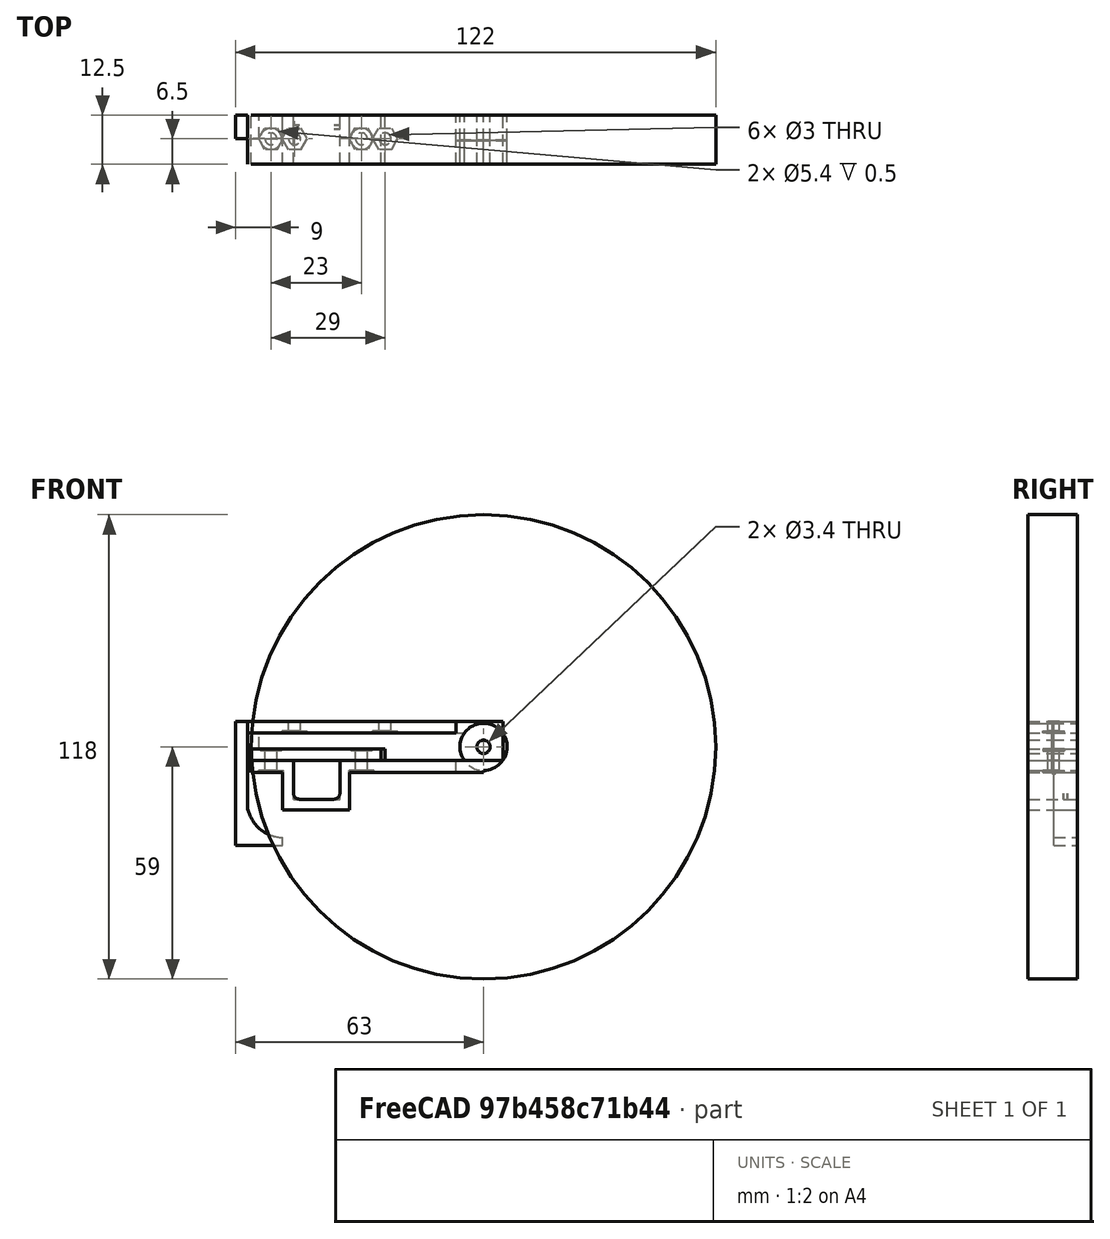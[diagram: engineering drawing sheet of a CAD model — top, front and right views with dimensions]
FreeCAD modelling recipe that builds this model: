
FCSTD DOCUMENT  (FreeCAD 0.18R16131 (Git))
Label: Soporte Motor 1
License: All rights reserved
LicenseURL: http://en.wikipedia.org/wiki/All_rights_reserved
objects: Part::Box×13, Part::Cylinder×13, Part::MultiFuse×11, Part::Cut×11, Part::Extrusion×6, Part::RegularPolygon×4, Part::Circle×2, Part::Fillet×1
note: 61 computed .brp shape members not serialized (recipe doc carries the construction recipe); baked Part::Feature solids carry a one-line shape summary decoded from their .brp

FEATURE [Part::Box] Box  label="Cubo"
  AttacherType = Attacher::AttachEngine3D
  Height = 12.6
  Length = 17
  Placement = pos=(-1,0,-1) rot=(0,0,1;0rad)
  Width = 12.5
FEATURE [Part::Box] Box001  label="Cubo001"
  AttacherType = Attacher::AttachEngine3D
  Height = 10
  Length = 11.8
  Placement = pos=(1.7,0,1.7) rot=(0,0,1;0rad)
  Width = 12.5
FEATURE [Part::Fillet] Fillet
  Base = -> Box001
  Edges = 2 edges r=1.5: [Edge4,Edge8]
FEATURE [Part::Box] Box002  label="Cubo002"
  AttacherType = Attacher::AttachEngine3D
  Height = 10
  Length = 11.8
  Placement = pos=(1.7,9,1.7) rot=(0,0,1;0rad)
  Width = 1
FEATURE [Part::Box] Box003  label="Cubo003"
  AttacherType = Attacher::AttachEngine3D
  Height = 10
  Length = 65
  Placement = pos=(-10,0,11.5) rot=(0,0,1;0rad)
  Width = 12.5
FEATURE [Part::Cylinder] Cylinder  label="Eje 1"
  Angle = 360
  AttacherType = Attacher::AttachEngine3D
  Height = 3
  Placement = pos=(50,0,15) rot=(-1,0,0;1.5708rad)
  Radius = 6
FEATURE [Part::Box] Box004  label="Cubo004"
  AttacherType = Attacher::AttachEngine3D
  Height = 3
  Length = 59
  Placement = pos=(-9,0,8.5) rot=(0,0,1;0rad)
  Width = 12.5
FEATURE [Part::Box] Box005  label="Cubo005"
  AttacherType = Attacher::AttachEngine3D
  Height = 3
  Length = 53
  Placement = pos=(-10,0,18.5) rot=(0,0,1;0rad)
  Width = 12.5
FEATURE [Part::Box] Box006  label="Cubo006"
  AttacherType = Attacher::AttachEngine3D
  Height = 3
  Length = 35
  Placement = pos=(-10,0,11.5) rot=(0,0,1;0rad)
  Width = 12.5
FEATURE [Part::Box] Box007  label="Tapa sin taladros"
  AttacherType = Attacher::AttachEngine3D
  Height = 3
  Length = 33
  Placement = pos=(-9,0,11.5) rot=(0,0,1;0rad)
  Width = 12.5
FEATURE [Part::Cylinder] Cylinder001  label="Taladro 1"
  Angle = 360
  AttacherType = Attacher::AttachEngine3D
  Height = 24
  Placement = pos=(-4,6.5,0) rot=(0,0,1;0rad)
  Radius = 1.5
FEATURE [Part::Cylinder] Cylinder002  label="Taladro 2"
  Angle = 360
  AttacherType = Attacher::AttachEngine3D
  Height = 24
  Placement = pos=(19,6.5,0) rot=(0,0,1;0rad)
  Radius = 1.5
FEATURE [Part::Box] Box008  label="Cubo008"
  AttacherType = Attacher::AttachEngine3D
  Height = 31.5
  Length = 3
  Placement = pos=(-13,3.2,-10) rot=(0,0,1;0rad)
  Width = 6
FEATURE [Part::Box] Box009  label="Cubo009"
  AttacherType = Attacher::AttachEngine3D
  Height = 9
  Length = 9
  Placement = pos=(-10,3.2,-10) rot=(0,0,1;0rad)
  Width = 6
FEATURE [Part::Box] Box010  label="Cubo010"
  AttacherType = Attacher::AttachEngine3D
  Height = 4
  Length = 3
  Placement = pos=(-10,3.2,14.5) rot=(0,0,1;0rad)
  Width = 6
FEATURE [Part::Cylinder] Cylinder003  label="Cilindro001"
  Angle = 360
  AttacherType = Attacher::AttachEngine3D
  Height = 12.5
  Placement = pos=(50,0,15) rot=(-1,0,0;1.5708rad)
  Radius = 59
FEATURE [Part::Cylinder] Cylinder004  label="Taladro 3"
  Angle = 360
  AttacherType = Attacher::AttachEngine3D
  Height = 20.5
  Placement = pos=(50,-3,15) rot=(-1,0,0;1.5708rad)
  Radius = 1.7
FEATURE [Part::Cylinder] Cylinder005  label="Eje 2"
  Angle = 360
  AttacherType = Attacher::AttachEngine3D
  Height = 3
  Placement = pos=(50,3,15) rot=(-1,0,0;1.5708rad)
  Radius = 6
FEATURE [Part::Cylinder] Cylinder006  label="Eje 3"
  Angle = 360
  AttacherType = Attacher::AttachEngine3D
  Height = 6.4
  Placement = pos=(50,6.1,15) rot=(-1,0,0;1.5708rad)
  Radius = 6
FEATURE [Part::Box] Box011  label="Cubo011"
  AttacherType = Attacher::AttachEngine3D
  Height = 3
  Length = 60
  Placement = pos=(-10,6.1,18.5) rot=(0,0,1;0rad)
  Width = 6.4
FEATURE [Part::MultiFuse] Fusion  label="Base superior"
  Shapes = -> [Box011,Box005,Cylinder006]
FEATURE [Part::Box] Box012  label="Ranura Eje"
  AttacherType = Attacher::AttachEngine3D
  Height = 3
  Length = 7
  Placement = pos=(43,6,8.5) rot=(0,0,1;0rad)
  Width = 6.5
FEATURE [Part::Cut] Cut
  Base = -> Box004
  Tool = -> Box012
FEATURE [Part::MultiFuse] Fusion001  label="Base Inferior"
  Shapes = -> [Cylinder,Cylinder005,Cut,Box]
FEATURE [Part::MultiFuse] Fusion002  label="Hueco Motor"
  Shapes = -> [Fillet,Box002]
FEATURE [Part::Cut] Cut001  label="Base Inferior 2"
  Base = -> Fusion001
  Tool = -> Fusion002
FEATURE [Part::MultiFuse] Fusion003  label="Trasera Superior"
  Placement = pos=(0,3.3,0) rot=(0,0,1;0rad)
  Shapes = -> [Box008,Box009,Box010]
FEATURE [Part::MultiFuse] Fusion004  label="Base Superior 2"
  Shapes = -> [Fusion,Fusion003]
FEATURE [Part::Cylinder] Cylinder007  label="Taladro 004"
  Angle = 360
  AttacherType = Attacher::AttachEngine3D
  Height = 20.5
  Placement = pos=(50,-3,15) rot=(-1,0,0;1.5708rad)
  Radius = 1.7
FEATURE [Part::Cut] Cut002  label="Base Superior con eje"
  Base = -> Fusion004
  Tool = -> Cylinder004
FEATURE [Part::Cut] Cut003  label="Base Inferior con eje"
  Base = -> Cut001
  Tool = -> Cylinder007
FEATURE [Part::Cylinder] Cylinder008  label="Taladro 1b"
  Angle = 360
  AttacherType = Attacher::AttachEngine3D
  Height = 24
  Placement = pos=(-4,6.5,0) rot=(0,0,1;0rad)
  Radius = 1.5
FEATURE [Part::Cylinder] Cylinder009  label="Taladro 1c"
  Angle = 360
  AttacherType = Attacher::AttachEngine3D
  Height = 24
  Placement = pos=(-4,6.5,0) rot=(0,0,1;0rad)
  Radius = 1.5
FEATURE [Part::Cylinder] Cylinder010  label="Taladro 2b"
  Angle = 360
  AttacherType = Attacher::AttachEngine3D
  Height = 24
  Placement = pos=(19,6.5,0) rot=(0,0,1;0rad)
  Radius = 1.5
FEATURE [Part::Cylinder] Cylinder011  label="Taladro 2c"
  Angle = 360
  AttacherType = Attacher::AttachEngine3D
  Height = 24
  Placement = pos=(19,6.5,0) rot=(0,0,1;0rad)
  Radius = 1.5
FEATURE [Part::MultiFuse] Fusion005  label="Taladros superiores"
  Placement = pos=(6,0,0) rot=(0,0,1;0rad)
  Shapes = -> [Cylinder001,Cylinder002]
FEATURE [Part::MultiFuse] Fusion006  label="Taladros inferiores"
  Shapes = -> [Cylinder008,Cylinder010]
FEATURE [Part::MultiFuse] Fusion007  label="Taladros tapa"
  Shapes = -> [Cylinder009,Cylinder011]
FEATURE [Part::Cut] Cut004  label="Base superior mal"
  Base = -> Cut002
  Tool = -> Fusion005
FEATURE [Part::Cut] Cut005  label="Base inferior taladrada"
  Base = -> Cut003
  Tool = -> Fusion006
FEATURE [Part::Cut] Cut006  label="Tapa taladrada"
  Base = -> Box007
  Tool = -> Fusion007
FEATURE [Part::Cylinder] Cylinder012  label="Cilindro"
  Angle = 360
  AttacherType = Attacher::AttachEngine3D
  Height = 20
  Placement = pos=(-1,0,1) rot=(-1,0,0;1.5708rad)
  Radius = 9
FEATURE [Part::Cut] Cut007  label="Base superior taladrada"
  Base = -> Cut004
  Tool = -> Cylinder012
FEATURE [Part::RegularPolygon] RegularPolygon  label="Polígono regular"
  AttacherType = Attacher::AttachEngine3D
  Circumradius = 3.15
  Placement = pos=(19,6.5,8) rot=(0,0,1;0rad)
  Polygon = 6
FEATURE [Part::RegularPolygon] RegularPolygon001  label="Polígono regular001"
  AttacherType = Attacher::AttachEngine3D
  Circumradius = 3.15
  Placement = pos=(-4,6.5,8) rot=(0,0,1;0rad)
  Polygon = 6
FEATURE [Part::Extrusion] Extrude  label="Agujero tuerca 1"
  Base = -> RegularPolygon
  Dir = (0,0,1)
  DirMode = 2
  FaceMakerClass = Part::FaceMakerBullseye
  LengthFwd = 1
  LengthRev = 0
  Solid = true
  Symmetric = false
FEATURE [Part::Extrusion] Extrude001  label="Agujero tuerca 2"
  Base = -> RegularPolygon001
  Dir = (0,0,1)
  DirMode = 2
  FaceMakerClass = Part::FaceMakerBullseye
  LengthFwd = 1
  LengthRev = 0
  Solid = true
  Symmetric = false
FEATURE [Part::MultiFuse] Fusion008
  Shapes = -> [Extrude,Extrude001]
FEATURE [Part::Cut] Cut008  label="Base inferior tuercas"
  Base = -> Cut005
  Tool = -> Fusion008
FEATURE [Part::Circle] Circle  label="Circunferencia"
  Angle0 = 0
  Angle1 = 360
  AttacherType = Attacher::AttachEngine3D
  Placement = pos=(-4,6.5,15) rot=(0,0,1;0rad)
  Radius = 2.7
FEATURE [Part::Circle] Circle001  label="Circunferencia001"
  Angle0 = 0
  Angle1 = 360
  AttacherType = Attacher::AttachEngine3D
  Placement = pos=(19,6.5,15) rot=(0,0,1;0rad)
  Radius = 2.7
FEATURE [Part::Extrusion] Extrude002
  Base = -> Circle
  Dir = (0,0,1)
  DirMode = 2
  FaceMakerClass = Part::FaceMakerBullseye
  LengthFwd = 1
  LengthRev = 0
  Solid = true
  Symmetric = false
FEATURE [Part::Extrusion] Extrude003
  Base = -> Circle001
  Dir = (0,0,1)
  DirMode = 2
  FaceMakerClass = Part::FaceMakerBullseye
  LengthFwd = 1
  LengthRev = 0
  Solid = true
  Symmetric = false
FEATURE [Part::MultiFuse] Fusion009
  Placement = pos=(0,0,-1) rot=(0,0,1;0rad)
  Shapes = -> [Extrude002,Extrude003]
FEATURE [Part::Cut] Cut009  label="Tapa con tornilleria"
  Base = -> Cut006
  Tool = -> Fusion009
FEATURE [Part::RegularPolygon] RegularPolygon002  label="Polígono regular002"
  AttacherType = Attacher::AttachEngine3D
  Circumradius = 3.15
  Placement = pos=(19,6.5,8) rot=(0,0,1;0rad)
  Polygon = 6
FEATURE [Part::Extrusion] Extrude004  label="Agujero tuerca 3"
  Base = -> RegularPolygon002
  Dir = (0,0,1)
  DirMode = 2
  FaceMakerClass = Part::FaceMakerBullseye
  LengthFwd = 1
  LengthRev = 0
  Placement = pos=(6,0,10) rot=(0,0,1;0rad)
  Solid = true
  Symmetric = false
FEATURE [Part::RegularPolygon] RegularPolygon003  label="Polígono regular003"
  AttacherType = Attacher::AttachEngine3D
  Circumradius = 3.15
  Placement = pos=(19,6.5,8) rot=(0,0,1;0rad)
  Polygon = 6
FEATURE [Part::Extrusion] Extrude005  label="Agujero tuerca 4"
  Base = -> RegularPolygon003
  Dir = (0,0,1)
  DirMode = 2
  FaceMakerClass = Part::FaceMakerBullseye
  LengthFwd = 1
  LengthRev = 0
  Placement = pos=(-17,0,10) rot=(0,0,1;0rad)
  Solid = true
  Symmetric = false
FEATURE [Part::MultiFuse] Fusion010
  Shapes = -> [Extrude004,Extrude005]
FEATURE [Part::Cut] Cut010  label="Base superior tuercas"
  Base = -> Cut007
  Tool = -> Fusion010
